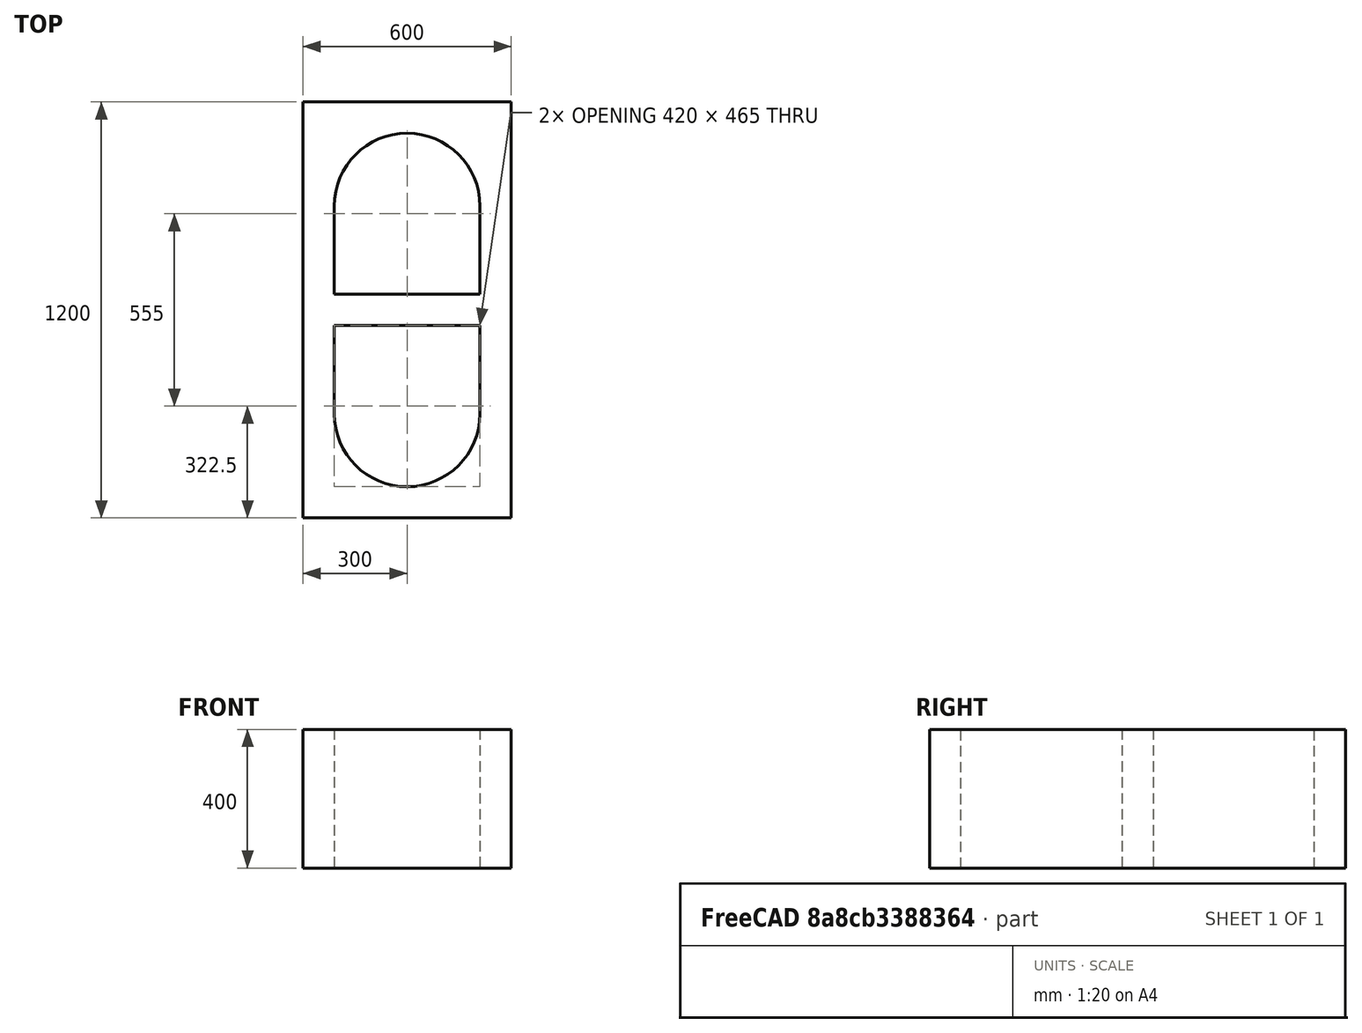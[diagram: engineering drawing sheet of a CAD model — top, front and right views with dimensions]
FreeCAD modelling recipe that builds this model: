
FCSTD DOCUMENT  (FreeCAD 0.19R22284 (Git))
Label: trarund
License: All rights reserved
LicenseURL: http://en.wikipedia.org/wiki/All_rights_reserved
objects: Sketcher::SketchObject×2, PartDesign::Pad×1, PartDesign::Pocket×1, PartDesign::Body×1, Fem::FemSolverObjectPython×1, Fem::FemMeshShapeNetgenObject×1, Fem::FemAnalysis×1
note: 7 computed .brp shape members not serialized (recipe doc carries the construction recipe); baked Part::Feature solids carry a one-line shape summary decoded from their .brp

FEATURE [Sketcher::SketchObject] Sketch
  MapMode = 5
  Placement = pos=(0,0,0) rot=(1,0,0;1.5708rad)
  Support = -> [XZ_Plane]
  sketch-geometry (4):
    g0: LineSegment StartX=-300 StartY=200 StartZ=0 EndX=300 EndY=200 EndZ=0
    g1: LineSegment StartX=300 StartY=200 StartZ=0 EndX=300 EndY=-200 EndZ=0
    g2: LineSegment StartX=300 StartY=-200 StartZ=0 EndX=-300 EndY=-200 EndZ=0
    g3: LineSegment StartX=-300 StartY=-200 StartZ=0 EndX=-300 EndY=200 EndZ=0
  constraints (10):
    c: Coincident(g0,g1)
    c: Coincident(g1,g2)
    c: Coincident(g2,g3)
    c: Coincident(g3,g0)
    c: Horizontal(g2)
    c: Vertical(g3)
    c: Symmetric(g0,g0,g-2)
    c: Symmetric(g0,g1,g-1)
    c: DistanceX(g2,g2) = 600
    c: DistanceY(g3,g3) = 400
FEATURE [PartDesign::Pad] Pad
  Length = 1200
  Length2 = 100
  Placement = pos=(0,0,0) rot=(1,0,0;1.5708rad)
  Profile = -> Sketch
  Type = 0
FEATURE [Sketcher::SketchObject] Sketch001
  ExternalGeometry = -> [Pad]
  MapMode = 5
  Placement = pos=(0,1.332e-13,200) rot=(0,0,1;3.14159rad)
  Support = -> [Pad]
  sketch-geometry (15):
    g0: LineSegment StartX=-210 StartY=900 StartZ=0 EndX=-210 EndY=645 EndZ=0
    g1: LineSegment StartX=210 StartY=900 StartZ=0 EndX=210 EndY=645 EndZ=0
    g2: ArcOfCircle CenterX=-1.25e-14 CenterY=900 CenterZ=0 NormalX=0 NormalY=0 NormalZ=1 AngleXU=0 Radius=210 StartAngle=0 EndAngle=3.14159
    g3: ArcOfCircle CenterX=-8.6e-15 CenterY=300 CenterZ=0 NormalX=0 NormalY=0 NormalZ=1 AngleXU=0 Radius=210 StartAngle=3.14159 EndAngle=6.28319
    g4: GeomPoint X=0 Y=1110 Z=0
    g5: LineSegment [constr] StartX=-210 StartY=900 StartZ=0 EndX=-300 EndY=900 EndZ=0
    g6: LineSegment [constr] StartX=0 StartY=1110 StartZ=0 EndX=0 EndY=1200 EndZ=0
    g7: GeomPoint X=0 Y=90 Z=0
    g8: LineSegment [constr] StartX=0 StartY=90 StartZ=0 EndX=0 EndY=0 EndZ=0
    g9: LineSegment [constr] StartX=-300 StartY=600 StartZ=0 EndX=300 EndY=600 EndZ=0
    g10: LineSegment StartX=-210 StartY=645 StartZ=0 EndX=210 EndY=645 EndZ=0
    g11: LineSegment StartX=-210 StartY=555 StartZ=0 EndX=210 EndY=555 EndZ=0
    g12: LineSegment StartX=-210 StartY=555 StartZ=0 EndX=-210 EndY=300 EndZ=0
    g13: LineSegment StartX=210 StartY=555 StartZ=0 EndX=210 EndY=300 EndZ=0
    g14: LineSegment [constr] StartX=210 StartY=645 StartZ=0 EndX=210 EndY=555 EndZ=0
  constraints (40):
    c: Vertical(g0)
    c: Coincident(g2,g0)
    c: Coincident(g2,g1)
    c: Coincident(g3,g12)
    c: Coincident(g3,g13)
    c: Symmetric(g0,g1,g-2)
    c: Symmetric(g13,g12,g-2)
    c: PointOnObject(g4,g-2)
    c: PointOnObject(g4,g2)
    c: Coincident(g5,g0)
    c: PointOnObject(g5,g-3)
    c: Coincident(g6,g4)
    c: PointOnObject(g6,g-4)
    c: Perpendicular(g5,g-3)
    c: Vertical(g6)
    c: Equal(g5,g6)
    c: Horizontal(g3,g13)
    c: Horizontal(g2,g1)
    c: PointOnObject(g7,g-2)
    c: PointOnObject(g7,g3)
    c: Coincident(g8,g7)
    c: Coincident(g8,g-1)
    c: Equal(g8,g5)
    c: Distance(g5) = 90
    c: PointOnObject(g9,g-3)
    c: PointOnObject(g9,g-5)
    c: Symmetric(g6,g-1,g9)
    c: Horizontal(g10)
    c: PointOnObject(g11,g1)
    c: Horizontal(g11)
    c: Coincident(g0,g10)
    c: Tangent(g0,g12)
    c: Coincident(g1,g10)
    c: Tangent(g1,g13)
    c: PointOnObject(g12,g11)
    c: PointOnObject(g13,g11)
    c: Symmetric(g0,g11,g9)
    c: Coincident(g14,g1)
    c: Coincident(g14,g11)
    c: Equal(g5,g14)
FEATURE [PartDesign::Pocket] Pocket
  BaseFeature = -> Pad
  Length = 5
  Length2 = 100
  Placement = pos=(0,0,0) rot=(1,0,0;1.5708rad)
  Profile = -> Sketch001
  Type = 1
FEATURE [PartDesign::Body] Body
  Group = -> [Sketch,Pad,Sketch001,Pocket]
  Origin = -> Origin
  Tip = -> Pocket
FEATURE [Fem::FemSolverObjectPython] SolverCcxTools  # FEM object (typed FeaturePython)
  AnalysisType = 0
  BeamShellResultOutput3D = false
  EigenmodeHighLimit = 1000000
  EigenmodeLowLimit = 0
  EigenmodesCount = 10
  GeometricalNonlinearity = 0
  IterationsControlParameterCutb = 0.25,0.5,0.75,0.85,,,1.5,
  IterationsControlParameterIter = 4,8,9,200,10,400,,200,,
  IterationsControlParameterTimeUse = false
  IterationsThermoMechMaximum = 2000
  IterationsUserDefinedIncrementations = false
  IterationsUserDefinedTimeStepLength = false
  MaterialNonlinearity = 0
  MatrixSolverType = 0
  SplitInputWriter = false
  ThermoMechSteadyState = true
  TimeEnd = 1
  TimeInitialStep = 0.01
FEATURE [Fem::FemMeshShapeNetgenObject] FEMMeshNetgen
  Fineness = 2
  GrowthRate = 0.3
  MaxSize = 1000
  NbSegsPerEdge = 1
  NbSegsPerRadius = 2
  Optimize = true
  SecondOrder = true
  Shape = -> Body
FEATURE [Fem::FemAnalysis] Analysis
  Group = -> [SolverCcxTools,FEMMeshNetgen]
